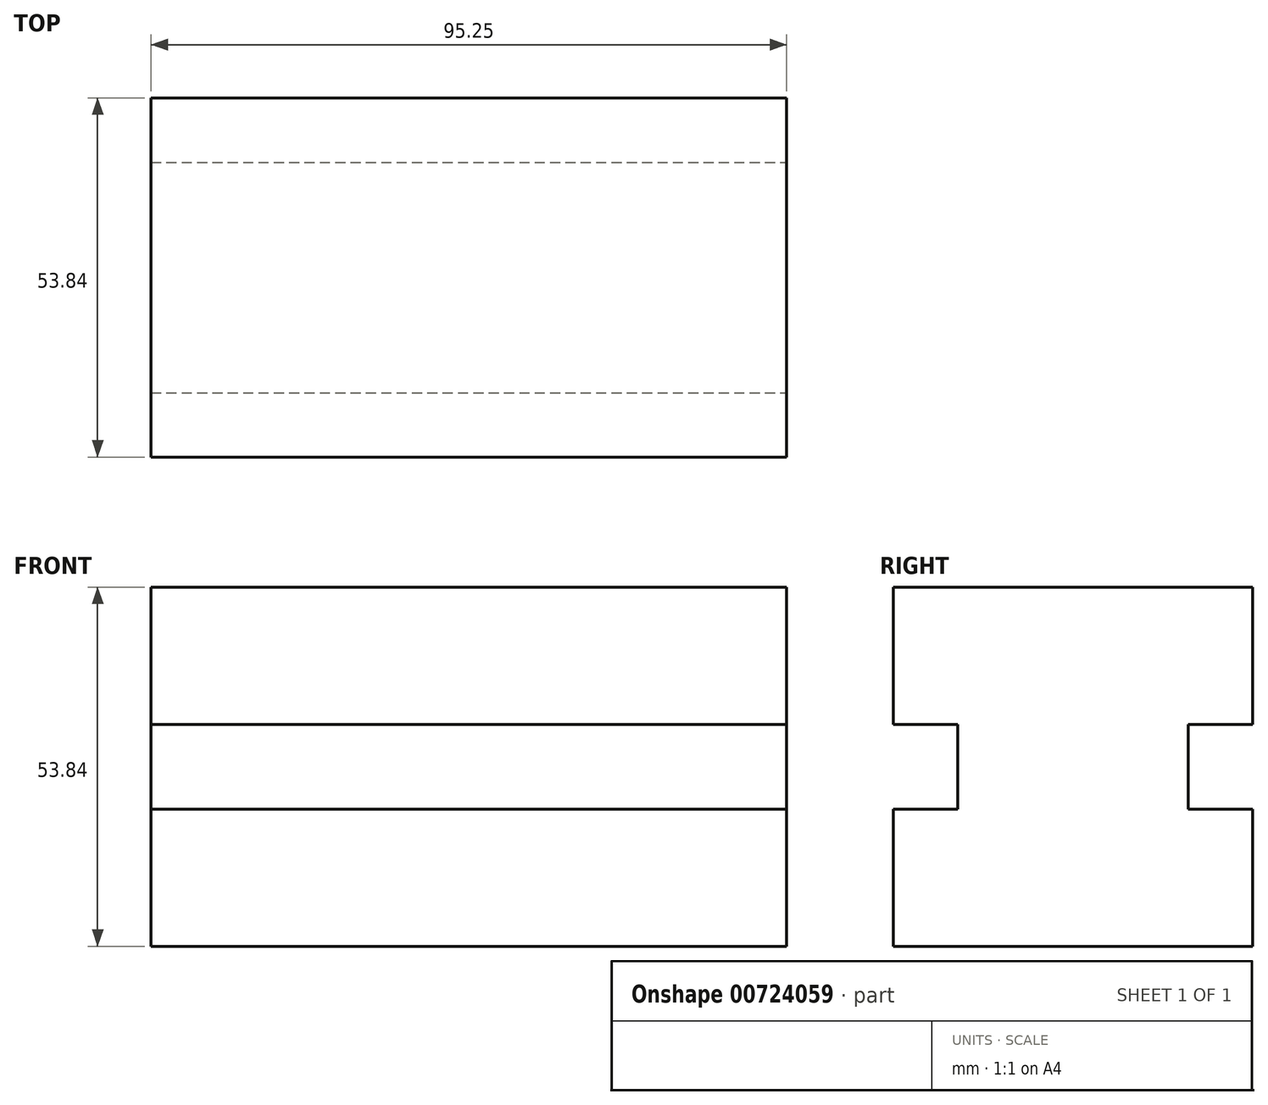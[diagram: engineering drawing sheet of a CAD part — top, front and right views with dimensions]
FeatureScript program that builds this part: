
annotation { "Feature Type Name" : "Feature", "Feature Type Description" : "" }
export const myFeature = defineFeature(function(context is Context, id is Id, definition is map)
    precondition{}
    {
        {
            var Q0;
            Q0=qCreatedBy(makeId("Right.planeOp"),FACE);
            var sketch = newSketch(context, id + "F0", { "sketchPlane" : qUnion([Q0])});
            skLineSegment(sketch, "E0.bottom", {"start": v(26.92, -26.92) * mm, "end": v(-26.92, -26.92) * mm});
            skLineSegment(sketch, "E0.top", {"start": v(26.92, 26.92) * mm, "end": v(-26.92, 26.92) * mm});
            skLineSegment(sketch, "E0.left", {"start": v(26.92, -26.92) * mm, "end": v(26.92, -6.35) * mm});
            skLineSegment(sketch, "E0.right", {"start": v(-26.92, -26.92) * mm, "end": v(-26.92, -6.35) * mm});
            skPoint(sketch, "E0.middle", {"position": v(0, 0) * mm});
            skLineSegment(sketch, "E1.bottom", {"start": v(-26.92, 6.35) * mm, "end": v(-17.27, 6.35) * mm});
            skLineSegment(sketch, "E1.top", {"start": v(-26.92, -6.35) * mm, "end": v(-17.27, -6.35) * mm});
            skLineSegment(sketch, "E1.right", {"start": v(-17.27, 6.35) * mm, "end": v(-17.27, -6.35) * mm});
            skLineSegment(sketch, "E2.trimOffspring", {"start": v(-26.92, 6.35) * mm, "end": v(-26.92, 26.92) * mm});
            skLineSegment(sketch, "E3", {"start": v(0, 26.92) * mm, "end": v(0, -30.38) * mm, "construction": true});
            skLineSegment(sketch, "E4.MirrorCS", {"start": v(26.92, 6.35) * mm, "end": v(17.27, 6.35) * mm});
            skLineSegment(sketch, "E5.MirrorCS", {"start": v(17.27, 6.35) * mm, "end": v(17.27, -6.35) * mm});
            skLineSegment(sketch, "E6.MirrorCS", {"start": v(26.92, -6.35) * mm, "end": v(17.27, -6.35) * mm});
            skLineSegment(sketch, "E7.trimOffspring", {"start": v(26.92, 6.35) * mm, "end": v(26.92, 26.92) * mm});
            skSolve(sketch);
        }
        {
            var Q0;
            Q0=makeQuery(id+"F0.imprint","IMPRINT",FACE,{"disambiguationData":[TD([[makeQuery(id+"F0.imprint","IMPRINT",EDGE,{"derivedFrom":sQuery(id+"F0.wireOp",EDGE,"E0.bottom")}),-1.0]])]});
            extrude(context, id + "F1", {"entities" : qUnion([Q0]), "oppositeDirection" : true, "depth" : 95.25 * mm, "offsetDistance" : 25.4 * mm});
        }
    });
